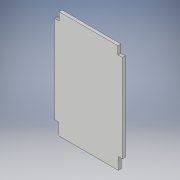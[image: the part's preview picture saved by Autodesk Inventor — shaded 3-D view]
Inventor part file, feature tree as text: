
AUTODESK INVENTOR PART (.ipt)
format: ipt  version: 2018 (Build 220112000, 112)  size: 105,472 bytes
history: native  units: in
note: dims shown in document units (in); Inventor stores cm internally (conversion verified against a paired STEP export)
features: sketch x2, extrude x1
ambient origin geometry x8: Origin, YZ Plane, XZ Plane, XY Plane, X Axis, Y Axis, Z Axis, Center Point
bodies: Solid1 (feature_tree)
feature tree (3):
  extrude  "Extrusion1"  Depth=1.0in
  sketch  "Sketch2"  dims[d2=22.0in d3=1.125in d4=2.0in d5=14.75in d6=1.125in d7=1.0in d8=0.75in d9=0.0in]
  sketch  "Sketch1"  dims[d0=3.0in d1=1.0in]
